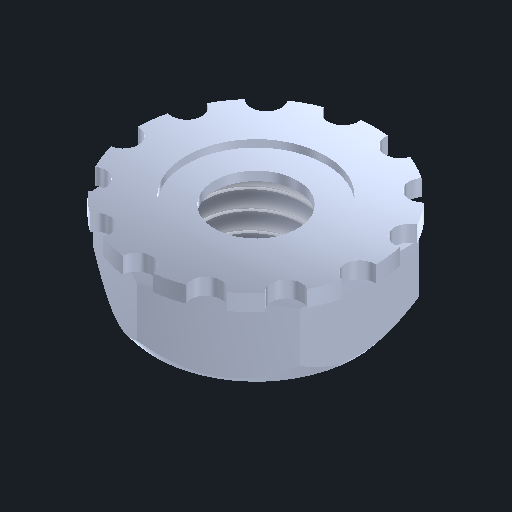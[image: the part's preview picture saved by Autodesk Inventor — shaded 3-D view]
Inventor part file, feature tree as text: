
AUTODESK INVENTOR PART (.ipt)
format: ipt  version: 2024 (Build 280153000, 153)  size: 304,640 bytes
history: native  units: in
note: dims shown in document units (in); Inventor stores cm internally (conversion verified against a paired STEP export)
features: other x2, imported_body x2, thread x1, extrude x1, projected_geometry x1
ambient origin geometry x8: Origin, YZ Plane, XZ Plane, XY Plane, X Axis, Y Axis, Z Axis, Center Point
bodies: Body1 (feature_tree), Body2 (feature_tree)
feature tree (7):
  parser-record x1  (decoder bookkeeping rows leaked as tree rows — omitted from the tree; the rows remain in map.json)
  imported_body  "Base1"
  imported_body  "Base2"
  thread  "Thread1"  [1 undecoded]
  extrude  "Extrusion1"  Depth=0.007in TaperAngle=0.0deg
  other  "NONE_1"
  projected_geometry  "Projected Loop1"
note: 1 required parameter value undecoded (feature->parameter linkage not recoverable at this tier; creation-order binding heuristic only, values carry confidence <= 0.55)
